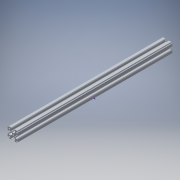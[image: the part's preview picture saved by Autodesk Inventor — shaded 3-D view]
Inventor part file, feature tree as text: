
AUTODESK INVENTOR PART (.ipt)
format: ipt  version: 2017 (Build 210142000, 142)  size: 461,312 bytes
history: native  units: in
note: dims shown in document units (in); Inventor stores cm internally (conversion verified against a paired STEP export)
features: sketch x5, extrude x3, other x3, reference x2, fillet x1
ambient origin geometry x8: Origin, YZ Plane, XZ Plane, XY Plane, X Axis, Y Axis, Z Axis, Center Point
bodies: Solid1 (feature_tree)
feature tree (14):
  extrude  "Extrusion1"  Depth=1.0in TaperAngle=0.0deg
  sketch  "Sketch3"  dims[d7=1.5in d8=0.0in]
  extrude  "Extrusion2"  [1 undecoded]
  extrude  "Extrusion3"  [1 undecoded]
  sketch  "Sketch6"
  sketch  "Sketch2"  dims[d0=57.0in d1=0.0in d5=1.0in d6=0.0in]
  sketch  "Sketch4"
  reference  "Reference1"
  sketch  "Sketch5"
  reference  "Reference2"
  fillet  "Fillet10"  [1 undecoded]
  other  "Robot Frame '16.iam"
  other  "Inline Cylinder Mount Bracket:1"
  other  "Inline Cylinder Mount Bracket:2"
note: 3 required parameter values undecoded (feature->parameter linkage not recoverable at this tier; creation-order binding heuristic only, values carry confidence <= 0.55)
